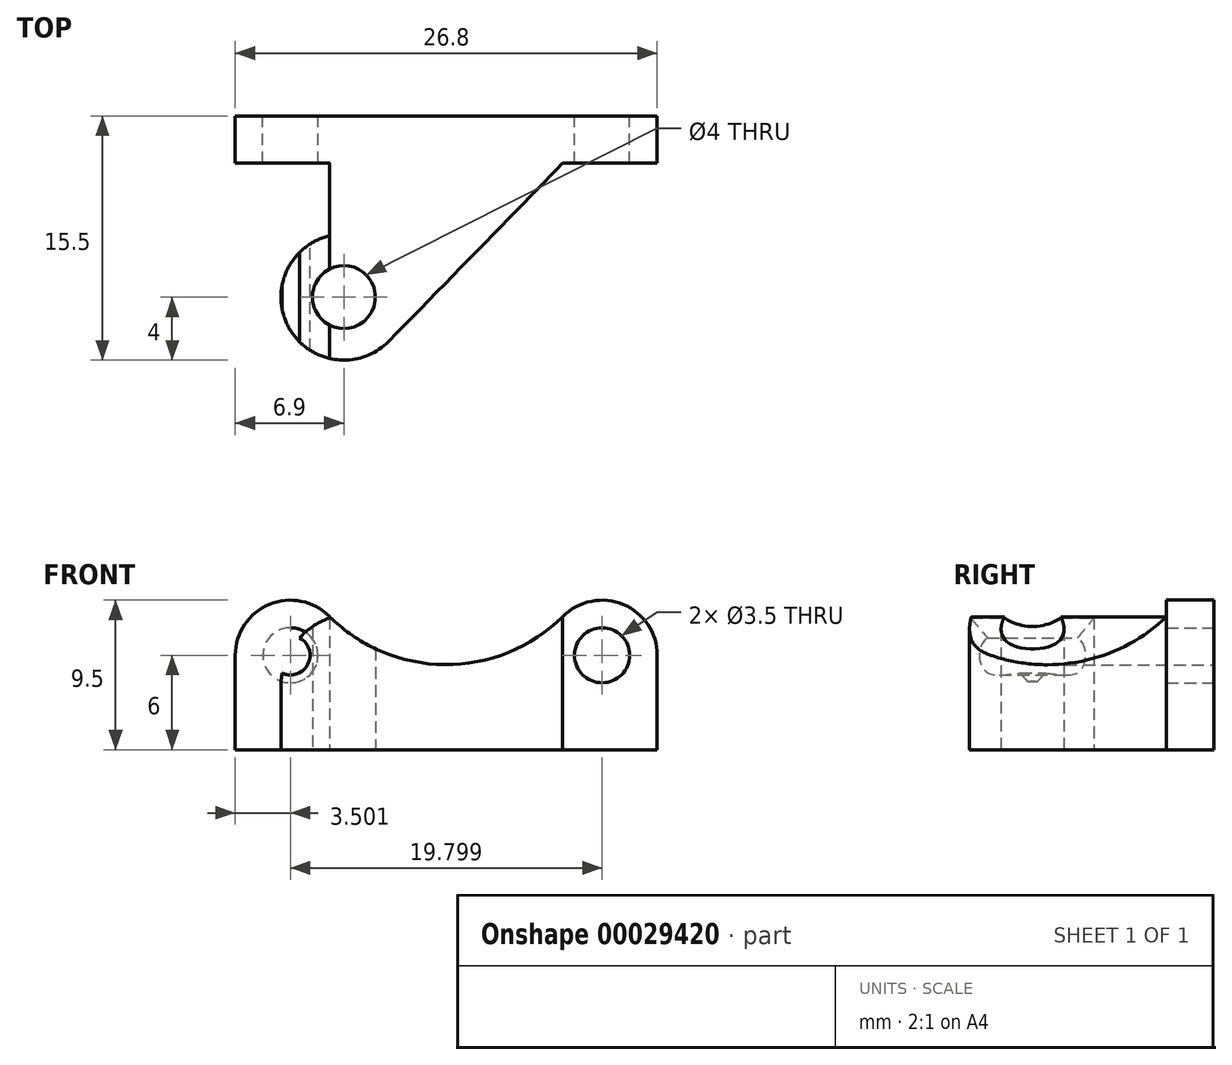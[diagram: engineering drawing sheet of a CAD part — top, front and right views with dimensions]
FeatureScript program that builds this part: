
annotation { "Feature Type Name" : "Feature", "Feature Type Description" : "" }
export const myFeature = defineFeature(function(context is Context, id is Id, definition is map)
    precondition{}
    {
        {
            var Q0;
            Q0=qCreatedBy(makeId("Front.planeOp"),FACE);
            var sketch = newSketch(context, id + "F0", { "sketchPlane" : qUnion([Q0])});
            skCircle(sketch, "E0", {"center": v(-9.9, 6) * mm, "radius": 1.75 * mm});
            skCircle(sketch, "E1", {"center": v(9.9, 6) * mm, "radius": 1.75 * mm});
            skCircle(sketch, "E2", {"center": v(0, 15.9) * mm, "radius": 10.5 * mm});
            skLineSegment(sketch, "E3", {"start": v(-9.9, 6) * mm, "end": v(9.9, 6) * mm, "construction": true});
            skPoint(sketch, "E4", {"position": v(0, 6) * mm});
            skCircle(sketch, "E5", {"center": v(0, 15.9) * mm, "radius": 14 * mm, "construction": true});
            skLineSegment(sketch, "E6", {"start": v(0, 0) * mm, "end": v(13.4, 0) * mm});
            skLineSegment(sketch, "E7", {"start": v(13.4, 0) * mm, "end": v(13.4, 6) * mm});
            skArc(sketch, "E8", {"start": v(13.4, 6) * mm, "mid": v(11.24, 9.23) * mm, "end": v(7.42, 8.47) * mm});
            skLineSegment(sketch, "E9", {"start": v(-9.9, 6) * mm, "end": v(0, 15.9) * mm, "construction": true});
            skLineSegment(sketch, "E10", {"start": v(9.9, 6) * mm, "end": v(0, 15.9) * mm, "construction": true});
            skLineSegment(sketch, "E11", {"start": v(0, 0) * mm, "end": v(0, -9.43) * mm, "construction": true});
            skArc(sketch, "E12.MirrorCS", {"start": v(-13.4, 6) * mm, "mid": v(-11.24, 9.23) * mm, "end": v(-7.42, 8.47) * mm});
            skLineSegment(sketch, "E13.MirrorCS", {"start": v(-13.4, 0) * mm, "end": v(-13.4, 6) * mm});
            skLineSegment(sketch, "E14.MirrorCS", {"start": v(0, 0) * mm, "end": v(-13.4, 0) * mm});
            skCircle(sketch, "E15", {"center": v(-9.9, 6) * mm, "radius": 1.25 * mm});
            skSolve(sketch);
        }
        {
            var Q0;
            Q0=makeQuery(id+"F0.imprint","IMPRINT",FACE,{"disambiguationData":[TD([[makeQuery(id+"F0.imprint","IMPRINT",EDGE,{"derivedFrom":sQuery(id+"F0.wireOp",EDGE,"E0")}),-1.0]])]});
            var Q1;
            Q1=makeQuery(id+"F0.imprint","IMPRINT",FACE,{"disambiguationData":[TD([[makeQuery(id+"F0.imprint","IMPRINT",EDGE,{"derivedFrom":sQuery(id+"F0.wireOp",EDGE,"E0")}),1.0]])]});
            extrude(context, id + "F1", {"entities" : qUnion([Q0, Q1]), "depth" : 20 * mm});
        }
        {
            var Q0;
            Q0=makeQuery(id+"F0.imprint","IMPRINT",FACE,{"disambiguationData":[TD([[makeQuery(id+"F0.imprint","IMPRINT",EDGE,{"derivedFrom":sQuery(id+"F0.wireOp",EDGE,"E0")}),1.0]])]});
            extrude(context, id + "F2", {"entities" : qUnion([Q0]), "operationType" : NewBodyOperationType.REMOVE, "depth" : 5 * mm});
        }
        {
            var Q0;
            Q0=qCreatedBy(makeId("Top.planeOp"),FACE);
            var sketch = newSketch(context, id + "F3", { "sketchPlane" : qUnion([Q0])});
            skCircle(sketch, "E16", {"center": v(-6.5, -11.5) * mm, "radius": 2 * mm});
            skLineSegment(sketch, "E17.0.0", {"start": v(-13.4, 0) * mm, "end": v(13.4, 0) * mm});
            skLineSegment(sketch, "E17.0.1", {"start": v(13.4, 0) * mm, "end": v(13.4, -20) * mm});
            skLineSegment(sketch, "E17.0.2", {"start": v(13.4, -20) * mm, "end": v(-13.4, -20) * mm});
            skLineSegment(sketch, "E17.0.3", {"start": v(-13.4, -20) * mm, "end": v(-13.4, 0) * mm});
            skLineSegment(sketch, "E18", {"start": v(13.4, -3) * mm, "end": v(7.4, -3) * mm});
            skLineSegment(sketch, "E19", {"start": v(-13.4, -3) * mm, "end": v(-7.4, -3) * mm});
            skLineSegment(sketch, "E20", {"start": v(-7.4, -3) * mm, "end": v(-7.4, -7.6) * mm});
            skCircle(sketch, "E21", {"center": v(-6.5, -11.5) * mm, "radius": 4 * mm});
            skLineSegment(sketch, "E22", {"start": v(-3.64, -14.3) * mm, "end": v(7.4, -3) * mm});
            skLineSegment(sketch, "E23", {"start": v(-7.4, -3) * mm, "end": v(7.4, -3) * mm, "construction": true});
            skLineSegment(sketch, "E24", {"start": v(-6.5, -11.5) * mm, "end": v(-6.5, -15.5) * mm, "construction": true});
            skSolve(sketch);
        }
        {
            var Q0;
            {var subQ4=sQuery(id+"F3.wireOp",EDGE,"E18");Q0=makeQuery(id+"F3.imprint","IMPRINT",FACE,{"disambiguationData":[TD([[makeQuery(id+"F3.imprint","IMPRINT",EDGE,{"derivedFrom":subQ4}),1.0]])]});}
            var Q1;
            {var subQ4=sQuery(id+"F3.wireOp",EDGE,"E19");Q1=makeQuery(id+"F3.imprint","IMPRINT",FACE,{"disambiguationData":[TD([[makeQuery(id+"F3.imprint","IMPRINT",EDGE,{"derivedFrom":subQ4}),-1.0]])]});}
            var Q2;
            Q2=makeQuery(id+"F3.imprint","IMPRINT",FACE,{"disambiguationData":[TD([[makeQuery(id+"F3.imprint","IMPRINT",EDGE,{"derivedFrom":sQuery(id+"F3.wireOp",EDGE,"E16")}),1.0]])]});
            extrude(context, id + "F4", {"entities" : qUnion([Q0, Q1, Q2]), "operationType" : NewBodyOperationType.REMOVE, "depth" : 25 * mm});
        }
        {
            var Q0;
            Q0=makeQuery(id+"F4.boolean.opBoolean","COPY",FACE,{"derivedFrom":makeQuery(id+"F4.opExtrude","SWEPT_FACE",FACE,{"disambiguationData":[OSD([sQuery(id+"F3.wireOp",EDGE,"E19")])]})});
            var sketch = newSketch(context, id + "F5", { "sketchPlane" : qUnion([Q0])});
            skArc(sketch, "E25.0.0", {"start": v(-7.4, 8.45) * mm, "mid": v(-7.41, 8.46) * mm, "end": v(-7.42, 8.47) * mm});
            skArc(sketch, "E25.0.1", {"start": v(-7.42, 8.47) * mm, "mid": v(-11.24, 9.23) * mm, "end": v(-13.4, 6) * mm});
            skLineSegment(sketch, "E25.0.2", {"start": v(-13.4, 6) * mm, "end": v(-13.4, 0) * mm});
            skLineSegment(sketch, "E25.0.3", {"start": v(-13.4, 0) * mm, "end": v(-7.4, 0) * mm});
            skLineSegment(sketch, "E25.0.4", {"start": v(-7.4, 0) * mm, "end": v(-7.4, 8.45) * mm});
            skLineSegment(sketch, "E26", {"start": v(-10.5, 4) * mm, "end": v(-13.4, 4) * mm});
            skLineSegment(sketch, "E27", {"start": v(-10.5, 0) * mm, "end": v(-10.5, 8.24) * mm});
            skArc(sketch, "E28", {"start": v(-7, 8.5) * mm, "mid": v(-9.52, 6.85) * mm, "end": v(-10.5, 4) * mm});
            skSolve(sketch);
        }
        {
            var Q0;
            {var subQ9=sQuery(id+"F5.wireOp",EDGE,"E25.0.0");Q0=makeQuery(id+"F5.imprint","IMPRINT",FACE,{"disambiguationData":[TD([[makeQuery(id+"F5.imprint","IMPRINT",EDGE,{"derivedFrom":subQ9}),1.0]])]});}
            var Q1;
            {var subQ0=makeQuery(id+"F4.boolean.opBoolean","INTERSECT",EDGE,{"derivedFrom":[makeQuery(id+"F1.opExtrude","SWEPT_FACE",FACE,{"disambiguationData":[OSD([sQuery(id+"F0.wireOp",EDGE,"E0")])]}),makeQuery(id+"F4.opExtrude","SWEPT_FACE",FACE,{"disambiguationData":[OSD([sQuery(id+"F3.wireOp",EDGE,"E19")])]})]});var subQ3=sQuery(id+"F5.wireOp",EDGE,"E27");var subQ6=makeQuery(id+"F5.imprint","INTERSECT",VERTEX,{"disambiguationData":[OD(0.0)],"derivedFrom":[subQ0,subQ3]});Q1=makeQuery(id+"F5.imprint","IMPRINT",FACE,{"disambiguationData":[TD([[makeQuery(id+"F5.imprint","IMPRINT",EDGE,{"disambiguationData":[TD([[subQ6,1.0]])],"derivedFrom":subQ3}),-1.0]])]});}
            var Q2;
            {var subQ0=makeQuery(id+"F4.boolean.opBoolean","INTERSECT",EDGE,{"derivedFrom":[makeQuery(id+"F1.opExtrude","SWEPT_FACE",FACE,{"disambiguationData":[OSD([sQuery(id+"F0.wireOp",EDGE,"E0")])]}),makeQuery(id+"F4.opExtrude","SWEPT_FACE",FACE,{"disambiguationData":[OSD([sQuery(id+"F3.wireOp",EDGE,"E19")])]})]});var subQ1=sQuery(id+"F5.wireOp",EDGE,"E27");var subQ3=makeQuery(id+"F5.imprint","INTERSECT",VERTEX,{"disambiguationData":[OD(0.0)],"derivedFrom":[subQ0,subQ1]});Q2=makeQuery(id+"F5.imprint","IMPRINT",FACE,{"disambiguationData":[TD([[makeQuery(id+"F5.imprint","IMPRINT",EDGE,{"disambiguationData":[TD([[subQ3,1.0]])],"derivedFrom":subQ1}),1.0]])]});}
            extrude(context, id + "F6", {"entities" : qUnion([Q0, Q1, Q2]), "operationType" : NewBodyOperationType.REMOVE, "depth" : 25 * mm});
        }
    });
